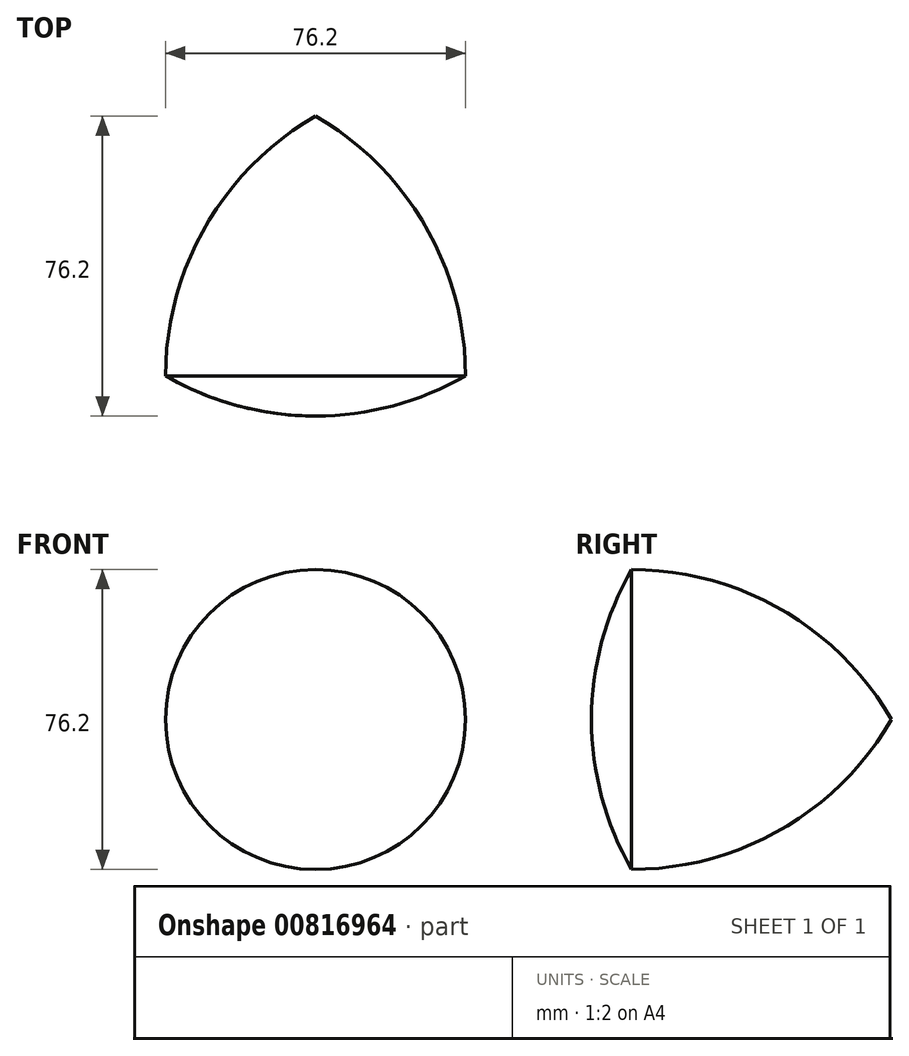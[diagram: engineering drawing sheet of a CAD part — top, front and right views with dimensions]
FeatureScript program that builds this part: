
annotation { "Feature Type Name" : "Feature", "Feature Type Description" : "" }
export const myFeature = defineFeature(function(context is Context, id is Id, definition is map)
    precondition{}
    {
        {
            var Q0;
            Q0=qCreatedBy(makeId("Top.planeOp"),FACE);
            var sketch = newSketch(context, id + "F0", { "sketchPlane" : qUnion([Q0])});
            skLineSegment(sketch, "E0", {"start": v(0, 0) * mm, "end": v(-38.1, -66) * mm});
            skLineSegment(sketch, "E1", {"start": v(-38.1, -66) * mm, "end": v(0, -66) * mm});
            skArc(sketch, "E2", {"start": v(-38.1, -66) * mm, "mid": v(-19.72, -73.6) * mm, "end": v(0, -76.2) * mm});
            skArc(sketch, "E3.trimOffspring", {"start": v(0, 0) * mm, "mid": v(-27.9, -27.9) * mm, "end": v(-38.1, -66) * mm});
            skLineSegment(sketch, "E4", {"start": v(0, 0) * mm, "end": v(0, -76.2) * mm});
            skSolve(sketch);
        }
        {
            var Q0;
            Q0 = qSketchRegion(id + "F0", true);
            var Q1;
            Q1=sQuery(id+"F0.wireOp",EDGE,"E4");
            revolve(context, id + "F1", {"surfaceOperationType" : NewSurfaceOperationType.NEW, "entities" : qUnion([Q0]), "axis" : qUnion([Q1]), "revolveType" : RevolveType.FULL});
        }
    });
